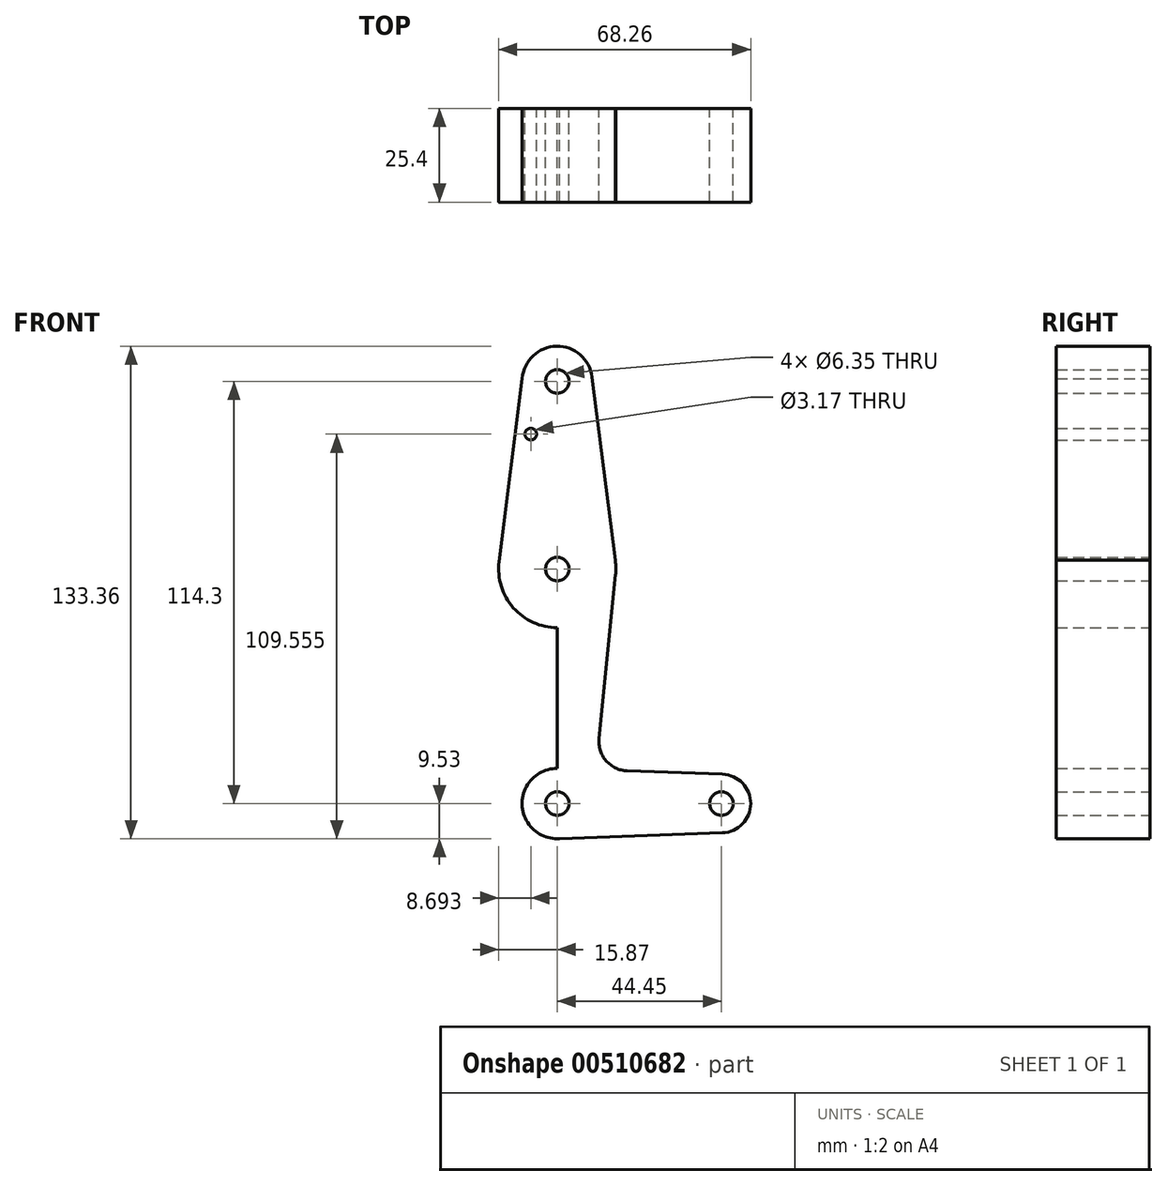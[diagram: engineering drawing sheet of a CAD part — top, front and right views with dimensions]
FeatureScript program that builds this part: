
annotation { "Feature Type Name" : "Feature", "Feature Type Description" : "" }
export const myFeature = defineFeature(function(context is Context, id is Id, definition is map)
    precondition{}
    {
        {
            var Q0;
            Q0=qCreatedBy(makeId("Front.planeOp"),FACE);
            var sketch = newSketch(context, id + "F0", { "sketchPlane" : qUnion([Q0])});
            skCircle(sketch, "E0", {"center": v(0, 0) * mm, "radius": 9.53 * mm});
            skCircle(sketch, "E1", {"center": v(0, 63.5) * mm, "radius": 15.88 * mm});
            skCircle(sketch, "E2", {"center": v(0, 114.3) * mm, "radius": 9.53 * mm});
            skCircle(sketch, "E3", {"center": v(44.45, 0) * mm, "radius": 7.94 * mm});
            skLineSegment(sketch, "E4", {"start": v(0, 114.3) * mm, "end": v(0, 63.5) * mm});
            skLineSegment(sketch, "E5", {"start": v(0, 0) * mm, "end": v(44.45, 0) * mm});
            skLineSegment(sketch, "E6", {"start": v(0, 63.5) * mm, "end": v(0, 0) * mm});
            skLineSegment(sketch, "E7", {"start": v(-9.4, 115.88) * mm, "end": v(-15.75, 65.49) * mm});
            skLineSegment(sketch, "E8", {"start": v(-15.75, 65.49) * mm, "end": v(-15.75, 61.51) * mm});
            skLineSegment(sketch, "E9", {"start": v(-15.75, 61.51) * mm, "end": v(-9.57, 0) * mm});
            skLineSegment(sketch, "E10", {"start": v(11.3, 17.6) * mm, "end": v(15.8, 61.9) * mm});
            skLineSegment(sketch, "E11", {"start": v(15.8, 61.9) * mm, "end": v(15.8, 65.1) * mm});
            skLineSegment(sketch, "E12", {"start": v(15.8, 65.1) * mm, "end": v(9.45, 115.49) * mm});
            skLineSegment(sketch, "E13", {"start": v(18.93, 8.85) * mm, "end": v(44.73, 7.93) * mm});
            skLineSegment(sketch, "E14", {"start": v(0, -9.53) * mm, "end": v(44.73, -7.93) * mm});
            skCircle(sketch, "E15", {"center": v(0, 114.3) * mm, "radius": 3.18 * mm});
            skCircle(sketch, "E16", {"center": v(0, 63.5) * mm, "radius": 3.18 * mm});
            skCircle(sketch, "E17", {"center": v(0, 0) * mm, "radius": 3.18 * mm});
            skCircle(sketch, "E18", {"center": v(44.45, 0) * mm, "radius": 3.18 * mm});
            skPoint(sketch, "E19.newPointB", {"position": v(9.52, 0) * mm});
            skArc(sketch, "E19.filletArc", {"start": v(11.3, 17.6) * mm, "mid": v(13.22, 11.57) * mm, "end": v(18.93, 8.85) * mm});
            skCircle(sketch, "E20", {"center": v(-7.18, 100.03) * mm, "radius": 1.59 * mm});
            skSolve(sketch);
        }
        {
            var Q0;
            Q0 = qSketchRegion(id + "F0", true);
            extrude(context, id + "F1", {"entities" : qUnion([Q0]), "depth" : 25.4 * mm, "offsetDistance" : 25.4 * mm});
        }
    });
